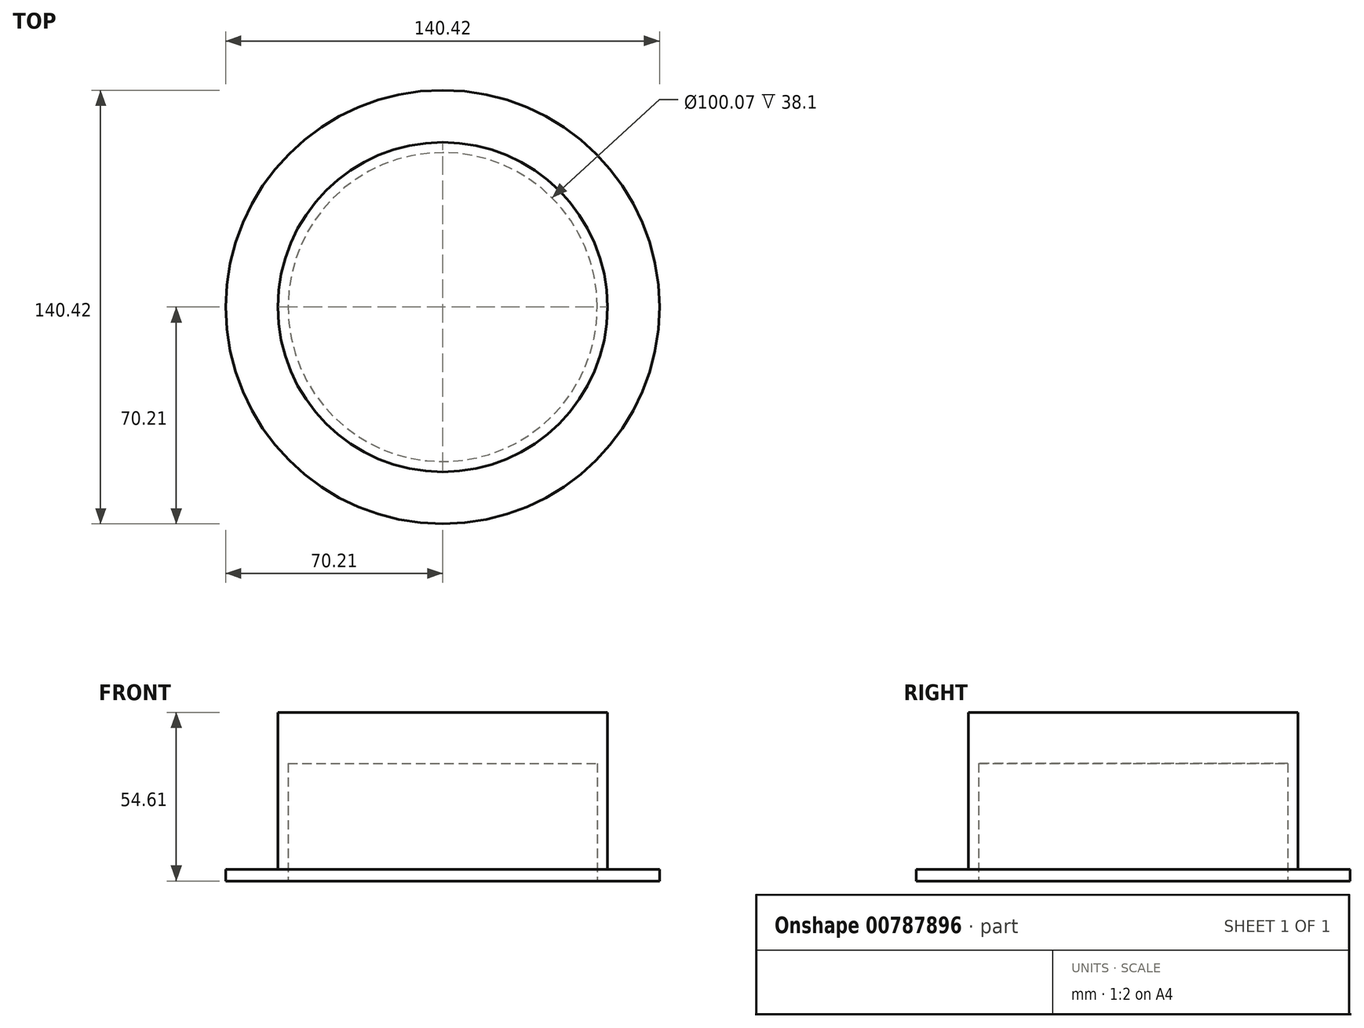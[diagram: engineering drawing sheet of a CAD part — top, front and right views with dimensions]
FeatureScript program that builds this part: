
annotation { "Feature Type Name" : "Feature", "Feature Type Description" : "" }
export const myFeature = defineFeature(function(context is Context, id is Id, definition is map)
    precondition{}
    {
        {
            var Q0;
            Q0=qCreatedBy(makeId("Top.planeOp"),FACE);
            var sketch = newSketch(context, id + "F0", { "sketchPlane" : qUnion([Q0])});
            skCircle(sketch, "E0", {"center": v(0, 0) * mm, "radius": 70.2 * mm});
            skSolve(sketch);
        }
        {
            var Q0;
            Q0=makeQuery(id+"F0.imprint","IMPRINT",FACE,{"disambiguationData":[TD([[makeQuery(id+"F0.imprint","IMPRINT",EDGE,{"derivedFrom":sQuery(id+"F0.wireOp",EDGE,"E0")}),1.0]])]});
            extrude(context, id + "F1", {"entities" : qUnion([Q0]), "depth" : 3.8 * mm, "offsetDistance" : 25.4 * mm});
        }
        {
            var Q0;
            Q0=makeQuery(id+"F1.opExtrude","CAP_FACE",FACE,{"disambiguationData":[OSD([sQuery(id+"F0.wireOp",EDGE,"E0")])],"isStart":false});
            var sketch = newSketch(context, id + "F2", { "sketchPlane" : qUnion([Q0])});
            skCircle(sketch, "E1", {"center": v(0, 0) * mm, "radius": 53.36 * mm});
            skSolve(sketch);
        }
        {
            var Q0;
            Q0 = qSketchRegion(id + "F2", true);
            extrude(context, id + "F3", {"entities" : qUnion([Q0]), "operationType" : NewBodyOperationType.ADD, "depth" : 50.8 * mm, "offsetDistance" : 25.4 * mm});
        }
        {
            var Q0;
            Q0=makeQuery(id+"F1.opExtrude","CAP_FACE",FACE,{"disambiguationData":[OSD([sQuery(id+"F0.wireOp",EDGE,"E0")])],"isStart":true});
            var sketch = newSketch(context, id + "F4", { "sketchPlane" : qUnion([Q0])});
            skCircle(sketch, "E2", {"center": v(0, 0) * mm, "radius": 50.03 * mm});
            skSolve(sketch);
        }
        {
            var Q0;
            Q0=makeQuery(id+"F4.imprint","IMPRINT",FACE,{"disambiguationData":[TD([[makeQuery(id+"F4.imprint","IMPRINT",EDGE,{"derivedFrom":sQuery(id+"F4.wireOp",EDGE,"E2")}),1.0]])]});
            extrude(context, id + "F5", {"entities" : qUnion([Q0]), "operationType" : NewBodyOperationType.REMOVE, "oppositeDirection" : true, "depth" : 38.1 * mm, "offsetDistance" : 25.4 * mm});
        }
    });
